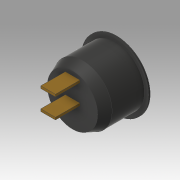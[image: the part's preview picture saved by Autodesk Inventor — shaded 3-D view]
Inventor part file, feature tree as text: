
AUTODESK INVENTOR PART (.ipt)
format: ipt  version: 2019.3 (Build 233278000, 278)  size: 215,552 bytes
history: native  units: mm
features: sketch x8, extrude x7, projected_geometry x3, revolve x1, fillet x1
ambient origin geometry x8: Origin, YZ Plane, XZ Plane, XY Plane, X Axis, Y Axis, Z Axis, Center Point
bodies: Solid1 (feature_tree)
feature tree (20):
  extrude  "Extrusion1"  Depth=2.0mm
  extrude  "Extrusion2"  Depth=10.8mm
  extrude  "Extrusion3"  Depth=11.0mm TaperAngle=0.0deg
  extrude  "Extrusion4"  Depth=5.0mm
  revolve  "Revolution1"  [1 undecoded]
  extrude  "Extrusion5"  Depth=23.0mm
  extrude  "Extrusion6"  Depth=9.25mm
  extrude  "Extrusion7"  Depth=1.0mm
  fillet  "Fillet1"  Radius=0.5mm
  sketch  "Sketch1"  dims[d0=20.0mm d1=2.0mm]
  sketch  "Sketch2"  dims[d2=0.8mm d3=10.8mm]
  sketch  "Sketch3"  dims[d4=1.0mm d5=11.0mm d6=0.0mm]
  sketch  "Sketch4"  dims[d7=3.5mm d8=-3.839724mm d9=5.0mm]
  sketch  "Sketch5"  dims[d10=0.8mm d11=6.0mm]
  projected_geometry  "Projected Loop1"
  sketch  "Sketch6"  dims[d12=8.4mm d13=0.0mm d14=23.0mm]
  projected_geometry  "Projected Loop2"
  sketch  "Sketch7"  dims[d15=2.0mm d16=0.0mm d17=9.25mm]
  sketch  "Sketch8"  dims[d18=1.0mm d19=1.0mm d20=0.5mm d21=90.0deg d22=17.0mm d23=0.2mm d24=0.0mm d25=16.75mm d26=4.0mm d27=-5.235988mm d28=4.0mm d29=0.0mm d30=0.5mm]
  projected_geometry  "Projected Loop3"
note: 1 required parameter value undecoded (feature->parameter linkage not recoverable at this tier; creation-order binding heuristic only, values carry confidence <= 0.55)
